# Revit family: KOMFORT EC SB
name_source: partatom
category: Mechanical Equipment
units: mm (PartAtom-declared; Revit-internal decimal feet)

## family parameters
Always vertical = Yes
Classification = None
Cut with Voids When Loaded = No
Part Type = Normal
Room Calculation Point = No
Round Connector Dimension = Use Diameter
Shared = No
Work Plane-Based = No

## types (16) — shared parameters
00_20_Manufacturer = Blauberg
00_20_Name = Air handling unit
Casing Material = Metal, painted, white, matt
Filter = G4, F7
Load Classification = HVAC
Maintenance zone material = <By Category>
Manufacturer = Blauberg
Number of Fase = 1
Temperature of moving air = -25…+40°C
URL = https://blaubergventilatoren.de
Voltage = 230 V
zero-valued in all types: Default Elevation

## per-type parameters (varying)
| type | Amperage | Apparent Load | B1 | D | Diameter | Dy | H1 | Height | L | L1 | L2 | Length | Maximum Air Flow | Power | Sound pressure level at 3 m distance | Weight | Width | h1 |
| KOMFORT EC SB 550 S21 | 2 A | 552 VA | 720 mm  [stored 2.3622 ft] | 200 mm  [stored 0.656168 ft] | 200 mm  [stored 0.656168 ft] | 190 mm | 675 mm  [stored 2.21457 ft] | 725 mm  [stored 2.37861 ft] | 823 mm  [stored 2.70013 ft] | 498 mm  [stored 1.63386 ft] | 288 mm  [stored 0.944882 ft] | 823 mm  [stored 2.70013 ft] | 690.0 m³/h | 337 W | 26 dBA | 82.00 kg | 720 mm  [stored 2.3622 ft] | 725 mm  [stored 2.37861 ft] |
| KOMFORT EC SB 350 S21 | 1 A | 322 VA | 583 mm | 160 mm  [stored 0.524934 ft] | 160 mm  [stored 0.524934 ft] | 150 mm | 675 mm  [stored 2.21457 ft] | 725 mm  [stored 2.37861 ft] | 730 mm  [stored 2.39501 ft] | 426 mm  [stored 1.39764 ft] | 230 mm  [stored 0.754593 ft] | 730 mm  [stored 2.39501 ft] | 450.0 m³/h | 178 W | 28 dBA | 64.00 kg | 583 mm | 725 mm  [stored 2.37861 ft] |
| KOMFORT EC S1B 350-E S21 | 1 A | 299 VA | 470 mm  [stored 1.54199 ft] | 160 mm  [stored 0.524934 ft] | 160 mm  [stored 0.524934 ft] | 150 mm | 675 mm  [stored 2.21457 ft] | 725 mm  [stored 2.37861 ft] | 730 mm  [stored 2.39501 ft] | 426 mm  [stored 1.39764 ft] | 200 mm  [stored 0.656168 ft] | 730 mm  [stored 2.39501 ft] | 420.0 m³/h | 169 W | 28 dBA | 57.00 kg | 470 mm  [stored 1.54199 ft] | 725 mm  [stored 2.37861 ft] |
| KOMFORT EC S 160 S21 | 1 A | 115 VA | 330 mm | 125 mm  [stored 0.410105 ft] | 125 mm  [stored 0.410105 ft] | 115 mm  [stored 0.377297 ft] | 550 mm | 600 mm  [stored 1.9685 ft] | 600 mm  [stored 1.9685 ft] | 388 mm  [stored 1.27297 ft] | 143 mm | 600 mm  [stored 1.9685 ft] | 200.0 m³/h | 57 W | 24 dBA | 34.00 kg | 330 mm | 600 mm  [stored 1.9685 ft] |
| KOMFORT EC S1 160 S21 | 1 A | 115 VA | 370 mm  [stored 1.21391 ft] | 125 mm  [stored 0.410105 ft] | 125 mm  [stored 0.410105 ft] | 115 mm  [stored 0.377297 ft] | 590 mm  [stored 1.9357 ft] | 640 mm  [stored 2.09974 ft] | 640 mm  [stored 2.09974 ft] | 388 mm  [stored 1.27297 ft] | 143 mm | 640 mm  [stored 2.09974 ft] | 200.0 m³/h | 57 W | 22 dBA | 42.00 kg | 370 mm  [stored 1.21391 ft] | 640 mm  [stored 2.09974 ft] |
| KOMFORT EC S1B 160 S21 | 1 A | 115 VA | 370 mm  [stored 1.21391 ft] | 125 mm  [stored 0.410105 ft] | 125 mm  [stored 0.410105 ft] | 115 mm  [stored 0.377297 ft] | 620 mm  [stored 2.03412 ft] | 670 mm  [stored 2.19816 ft] | 640 mm  [stored 2.09974 ft] | 388 mm  [stored 1.27297 ft] | 143 mm | 640 mm  [stored 2.09974 ft] | 200.0 m³/h | 57 W | 22 dBA | 44.00 kg | 370 mm  [stored 1.21391 ft] | 670 mm  [stored 2.19816 ft] |
| KOMFORT EC SB 160 S21 | 1 A | 115 VA | 330 mm | 125 mm  [stored 0.410105 ft] | 125 mm  [stored 0.410105 ft] | 115 mm  [stored 0.377297 ft] | 580 mm  [stored 1.90289 ft] | 630 mm  [stored 2.06693 ft] | 600 mm  [stored 1.9685 ft] | 388 mm  [stored 1.27297 ft] | 143 mm | 600 mm  [stored 1.9685 ft] | 200.0 m³/h | 57 W | 24 dBA | 36.00 kg | 330 mm | 630 mm  [stored 2.06693 ft] |
| KOMFORT EC SB 250 S21 | 1 A | 315 VA | 560 mm  [stored 1.83727 ft] | 160 mm  [stored 0.524934 ft] | 160 mm  [stored 0.524934 ft] | 150 mm | 970 mm  [stored 3.18241 ft] | 1020 mm  [stored 3.34646 ft] | 560 mm  [stored 1.83727 ft] | 390 mm  [stored 1.27953 ft] | 212 mm  [stored 0.695538 ft] | 560 mm  [stored 1.83727 ft] | 390.0 m³/h | 180 W | 35 dBA | 66.00 kg | 560 mm  [stored 1.83727 ft] | 1020 mm  [stored 3.34646 ft] |
| KOMFORT EC S1B 350 S21 | 1 A | 299 VA | 470 mm  [stored 1.54199 ft] | 160 mm  [stored 0.524934 ft] | 160 mm  [stored 0.524934 ft] | 150 mm | 675 mm  [stored 2.21457 ft] | 725 mm  [stored 2.37861 ft] | 730 mm  [stored 2.39501 ft] | 426 mm  [stored 1.39764 ft] | 200 mm  [stored 0.656168 ft] | 730 mm  [stored 2.39501 ft] | 420.0 m³/h | 169 W | 28 dBA | 57.00 kg | 470 mm  [stored 1.54199 ft] | 725 mm  [stored 2.37861 ft] |
| KOMFORT EC SB 350-E S21 | 1 A | 322 VA | 583 mm | 160 mm  [stored 0.524934 ft] | 160 mm  [stored 0.524934 ft] | 150 mm | 675 mm  [stored 2.21457 ft] | 725 mm  [stored 2.37861 ft] | 730 mm  [stored 2.39501 ft] | 426 mm  [stored 1.39764 ft] | 230 mm  [stored 0.754593 ft] | 730 mm  [stored 2.39501 ft] | 450.0 m³/h | 178 W | 28 dBA | 66.00 kg | 583 mm | 725 mm  [stored 2.37861 ft] |
| KOMFORT EC SB 550-E S21 | 2 A | 552 VA | 720 mm  [stored 2.3622 ft] | 200 mm  [stored 0.656168 ft] | 200 mm  [stored 0.656168 ft] | 190 mm | 675 mm  [stored 2.21457 ft] | 725 mm  [stored 2.37861 ft] | 823 mm  [stored 2.70013 ft] | 498 mm  [stored 1.63386 ft] | 288 mm  [stored 0.944882 ft] | 823 mm  [stored 2.70013 ft] | 690.0 m³/h | 337 W | 26 dBA | 82.00 kg | 720 mm  [stored 2.3622 ft] | 725 mm  [stored 2.37861 ft] |
| KOMFORT EC S 160-E S21 | 1 A | 115 VA | 330 mm | 125 mm  [stored 0.410105 ft] | 125 mm  [stored 0.410105 ft] | 115 mm  [stored 0.377297 ft] | 550 mm | 600 mm  [stored 1.9685 ft] | 600 mm  [stored 1.9685 ft] | 388 mm  [stored 1.27297 ft] | 143 mm | 600 mm  [stored 1.9685 ft] | 200.0 m³/h | 57 W | 24 dBA | 34.00 kg | 330 mm | 600 mm  [stored 1.9685 ft] |
| KOMFORT EC S1 160-E S21 | 1 A | 115 VA | 370 mm  [stored 1.21391 ft] | 125 mm  [stored 0.410105 ft] | 125 mm  [stored 0.410105 ft] | 115 mm  [stored 0.377297 ft] | 590 mm  [stored 1.9357 ft] | 640 mm  [stored 2.09974 ft] | 640 mm  [stored 2.09974 ft] | 388 mm  [stored 1.27297 ft] | 143 mm | 640 mm  [stored 2.09974 ft] | 200.0 m³/h | 57 W | 22 dBA | 42.00 kg | 370 mm  [stored 1.21391 ft] | 640 mm  [stored 2.09974 ft] |
| KOMFORT EC SB 160-E S21 | 1 A | 115 VA | 330 mm | 125 mm  [stored 0.410105 ft] | 125 mm  [stored 0.410105 ft] | 115 mm  [stored 0.377297 ft] | 580 mm  [stored 1.90289 ft] | 630 mm  [stored 2.06693 ft] | 600 mm  [stored 1.9685 ft] | 388 mm  [stored 1.27297 ft] | 143 mm | 600 mm  [stored 1.9685 ft] | 200.0 m³/h | 57 W | 24 dBA | 36.00 kg | 330 mm | 630 mm  [stored 2.06693 ft] |
| KOMFORT EC S1B 160-E S21 | 1 A | 115 VA | 370 mm  [stored 1.21391 ft] | 125 mm  [stored 0.410105 ft] | 125 mm  [stored 0.410105 ft] | 115 mm  [stored 0.377297 ft] | 620 mm  [stored 2.03412 ft] | 670 mm  [stored 2.19816 ft] | 640 mm  [stored 2.09974 ft] | 388 mm  [stored 1.27297 ft] | 143 mm | 640 mm  [stored 2.09974 ft] | 200.0 m³/h | 57 W | 22 dBA | 44.00 kg | 370 mm  [stored 1.21391 ft] | 670 mm  [stored 2.19816 ft] |
| KOMFORT EC SB 250-E S21 | 1 A | 315 VA | 560 mm  [stored 1.83727 ft] | 160 mm  [stored 0.524934 ft] | 160 mm  [stored 0.524934 ft] | 150 mm | 970 mm  [stored 3.18241 ft] | 1020 mm  [stored 3.34646 ft] | 560 mm  [stored 1.83727 ft] | 390 mm  [stored 1.27953 ft] | 212 mm  [stored 0.695538 ft] | 560 mm  [stored 1.83727 ft] | 390.0 m³/h | 180 W | 35 dBA | 66.00 kg | 560 mm  [stored 1.83727 ft] | 1020 mm  [stored 3.34646 ft] |

note: column(s) folded — value = type name in every type: 00_20_Type

note: [stored X ft] marks values corroborated as IEEE doubles in the binary element streams (Revit-internal decimal feet)
